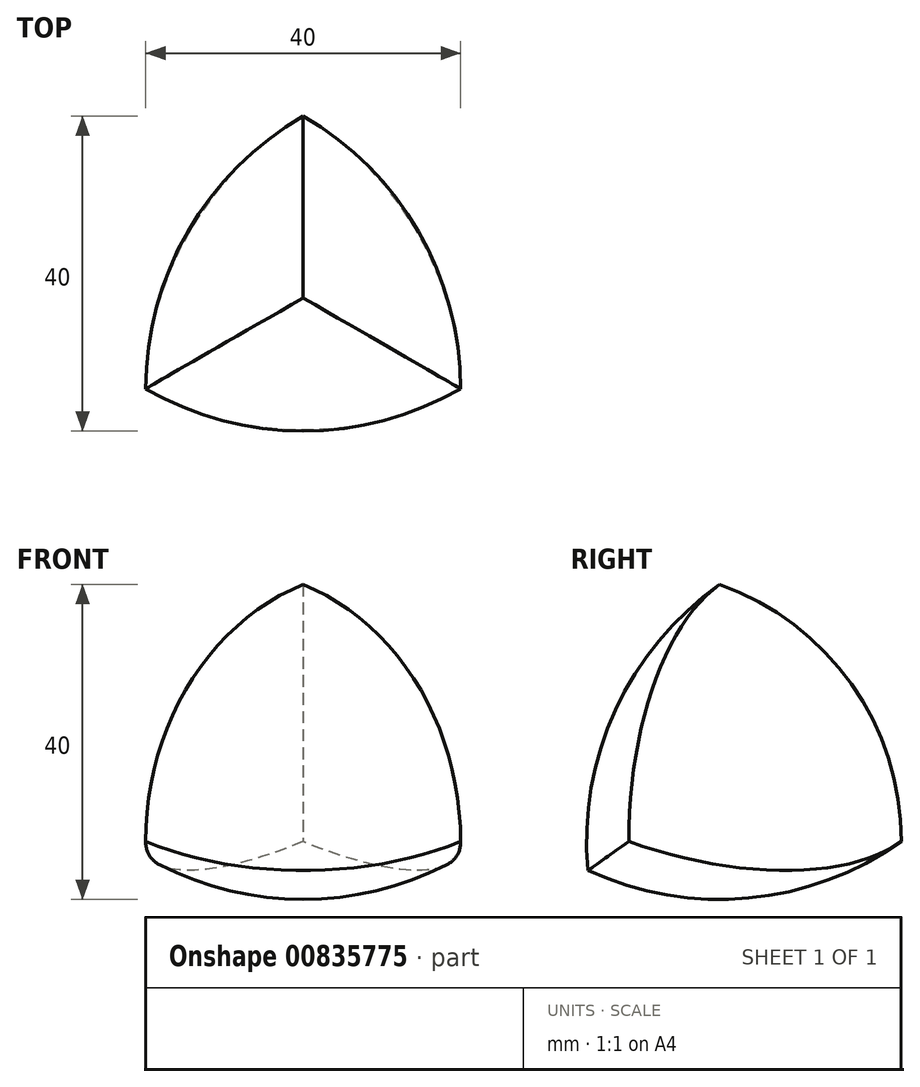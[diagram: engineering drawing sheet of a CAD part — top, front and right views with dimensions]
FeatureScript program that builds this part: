
annotation { "Feature Type Name" : "Feature", "Feature Type Description" : "" }
export const myFeature = defineFeature(function(context is Context, id is Id, definition is map)
    precondition{}
    {
        {
            var Q0;
            Q0=qCreatedBy(makeId("Top.planeOp"),FACE);
            var sketch = newSketch(context, id + "F0", { "sketchPlane" : qUnion([Q0])});
            skLineSegment(sketch, "E0", {"start": v(0, 23.1) * mm, "end": v(20, -11.55) * mm});
            skLineSegment(sketch, "E1", {"start": v(20, -11.55) * mm, "end": v(-20, -11.55) * mm});
            skLineSegment(sketch, "E2", {"start": v(-20, -11.55) * mm, "end": v(0, 23.1) * mm});
            skLineSegment(sketch, "E3", {"start": v(-20, -11.55) * mm, "end": v(10, 5.77) * mm, "construction": true});
            skLineSegment(sketch, "E4", {"start": v(0, 23.1) * mm, "end": v(0, -11.55) * mm, "construction": true});
            skLineSegment(sketch, "E5", {"start": v(20, -11.55) * mm, "end": v(-10, 5.77) * mm, "construction": true});
            skArc(sketch, "E6", {"start": v(0, 23.1) * mm, "mid": v(54.64, 8.45) * mm, "end": v(40, -46.19) * mm});
            skLineSegment(sketch, "E7", {"start": v(20, -11.55) * mm, "end": v(40, -46.19) * mm});
            skArc(sketch, "E8", {"start": v(20, -11.55) * mm, "mid": v(-20, -51.55) * mm, "end": v(-60, -11.55) * mm});
            skLineSegment(sketch, "E9", {"start": v(-20, -11.55) * mm, "end": v(-60, -11.55) * mm});
            skArc(sketch, "E10", {"start": v(-20, -11.55) * mm, "mid": v(-34.64, 43.1) * mm, "end": v(20, 57.74) * mm});
            skLineSegment(sketch, "E11", {"start": v(0, 23.1) * mm, "end": v(20, 57.74) * mm});
            skSolve(sketch);
        }
        {
            var Q0;
            Q0=qCreatedBy(makeId("Right.planeOp"),FACE);
            var sketch = newSketch(context, id + "F1", { "sketchPlane" : qUnion([Q0])});
            skLineSegment(sketch, "E12", {"start": v(0, 0) * mm, "end": v(0, 32.66) * mm, "construction": true});
            skLineSegment(sketch, "E13", {"start": v(0, 32.66) * mm, "end": v(23.1, 0) * mm});
            skArc(sketch, "E14", {"start": v(23.1, 0) * mm, "mid": v(32.66, 55.75) * mm, "end": v(-23.1, 65.32) * mm});
            skLineSegment(sketch, "E15", {"start": v(-23.1, 65.32) * mm, "end": v(0, 32.66) * mm});
            skSolve(sketch);
        }
        {
            var Q0;
            Q0=makeQuery(id+"F0.imprint","IMPRINT",FACE,{"disambiguationData":[TD([[makeQuery(id+"F0.imprint","IMPRINT",EDGE,{"derivedFrom":sQuery(id+"F0.wireOp",EDGE,"E0")}),1.0]])]});
            var Q1;
            Q1=sQuery(id+"F0.wireOp",EDGE,"E7");
            revolve(context, id + "F2", {"surfaceOperationType" : NewSurfaceOperationType.NEW, "entities" : qUnion([Q0]), "axis" : qUnion([Q1]), "revolveType" : RevolveType.FULL});
        }
        {
            var Q0;
            Q0=makeQuery(id+"F0.imprint","IMPRINT",FACE,{"disambiguationData":[TD([[makeQuery(id+"F0.imprint","IMPRINT",EDGE,{"derivedFrom":sQuery(id+"F0.wireOp",EDGE,"E1")}),1.0]])]});
            var Q1;
            Q1=sQuery(id+"F0.wireOp",EDGE,"E9");
            revolve(context, id + "F3", {"surfaceOperationType" : NewSurfaceOperationType.NEW, "entities" : qUnion([Q0]), "axis" : qUnion([Q1]), "revolveType" : RevolveType.FULL});
        }
        {
            var Q0;
            Q0=makeQuery(id+"F0.imprint","IMPRINT",FACE,{"disambiguationData":[TD([[makeQuery(id+"F0.imprint","IMPRINT",EDGE,{"derivedFrom":sQuery(id+"F0.wireOp",EDGE,"E2")}),1.0]])]});
            var Q1;
            Q1=sQuery(id+"F0.wireOp",EDGE,"E11");
            revolve(context, id + "F4", {"surfaceOperationType" : NewSurfaceOperationType.NEW, "entities" : qUnion([Q0]), "axis" : qUnion([Q1]), "revolveType" : RevolveType.FULL});
        }
        {
            var Q0;
            Q0=makeQuery(id+"F1.imprint","IMPRINT",FACE,{"disambiguationData":[TD([[makeQuery(id+"F1.imprint","IMPRINT",EDGE,{"derivedFrom":sQuery(id+"F1.wireOp",EDGE,"E13")}),1.0]])]});
            var Q1;
            Q1=sQuery(id+"F1.wireOp",EDGE,"E15");
            revolve(context, id + "F5", {"surfaceOperationType" : NewSurfaceOperationType.NEW, "entities" : qUnion([Q0]), "axis" : qUnion([Q1]), "revolveType" : RevolveType.FULL});
        }
        {
            var Q0;
            Q0=makeQuery(id+"F2.opRevolve","SWEPT_BODY",BODY,{"disambiguationData":[OSD([sQuery(id+"F0.wireOp",EDGE,"E0"),sQuery(id+"F0.wireOp",EDGE,"E6"),sQuery(id+"F0.wireOp",EDGE,"E7")])]});
            var Q1;
            Q1=makeQuery(id+"F3.opRevolve","SWEPT_BODY",BODY,{"disambiguationData":[OSD([sQuery(id+"F0.wireOp",EDGE,"E1"),sQuery(id+"F0.wireOp",EDGE,"E8"),sQuery(id+"F0.wireOp",EDGE,"E9")])]});
            var Q2;
            Q2=makeQuery(id+"F4.opRevolve","SWEPT_BODY",BODY,{"disambiguationData":[OSD([sQuery(id+"F0.wireOp",EDGE,"E2"),sQuery(id+"F0.wireOp",EDGE,"E10"),sQuery(id+"F0.wireOp",EDGE,"E11")])]});
            var Q3;
            Q3=makeQuery(id+"F5.opRevolve","SWEPT_BODY",BODY,{"disambiguationData":[OSD([sQuery(id+"F1.wireOp",EDGE,"E13"),sQuery(id+"F1.wireOp",EDGE,"E14"),sQuery(id+"F1.wireOp",EDGE,"E15")])]});
            booleanBodies(context, id + "F6", {"operationType" : BooleanOperationType.INTERSECTION, "tools" : qUnion([Q0, Q1, Q2, Q3])});
        }
    });
